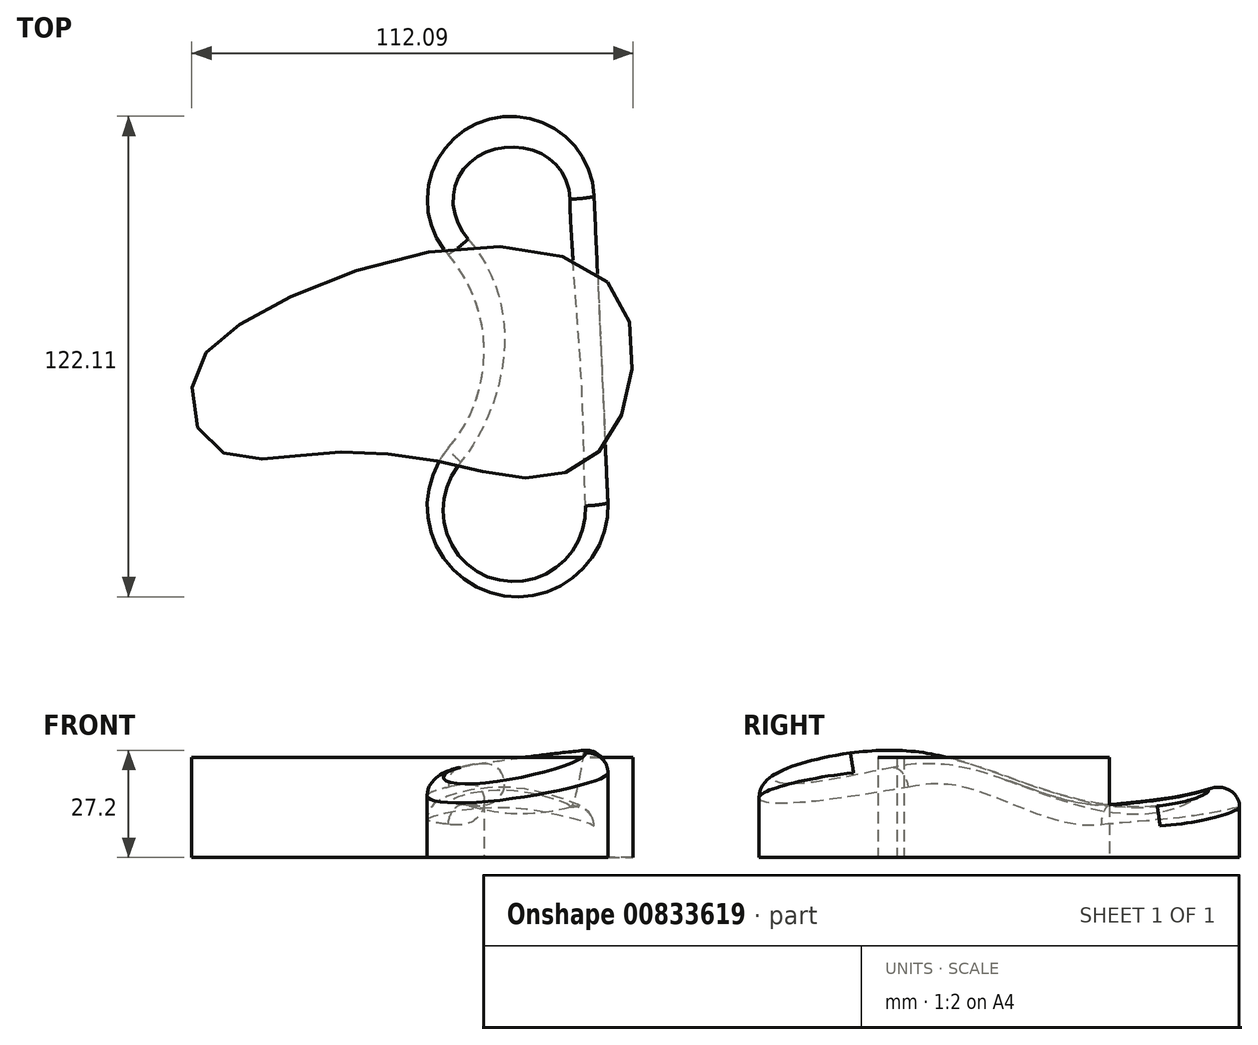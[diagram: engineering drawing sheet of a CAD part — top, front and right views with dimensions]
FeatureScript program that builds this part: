
annotation { "Feature Type Name" : "Feature", "Feature Type Description" : "" }
export const myFeature = defineFeature(function(context is Context, id is Id, definition is map)
    precondition{}
    {
        {
            var Q0;
            Q0=qCreatedBy(makeId("Right.planeOp"),FACE);
            cPlane(context, id + "F0", {"entities" : qUnion([Q0]), "cplaneType" : CPlaneType.OFFSET, "offset" : 25.4 * mm, "width" : 152.4 * mm, "height" : 152.4 * mm});
        }
        {
            var Q0;
            Q0=qCreatedBy(id+"F0.planeOp",FACE);
            cPlane(context, id + "F1", {"entities" : qUnion([Q0]), "cplaneType" : CPlaneType.OFFSET, "offset" : 25.4 * mm, "width" : 152.4 * mm, "height" : 152.4 * mm});
        }
        {
            var Q0;
            Q0=qCreatedBy(makeId("Right.planeOp"),FACE);
            var sketch = newSketch(context, id + "F2", { "sketchPlane" : qUnion([Q0])});
            skFitSpline(sketch, "E0", {"points": [v(-69.77, 10.75) * mm, v(-48.27, 16.65) * mm, v(-19.6, 21.71) * mm, v(13.28, 20.02) * mm, v(40.26, 17.5) * mm, v(69.77, 24.24) * mm], "startDerivative": vector(116.9, 33.43) * mm, "endDerivative": vector(144.91, 44.8) * mm});
            skLineSegment(sketch, "E1", {"start": v(-69.77, 10.75) * mm, "end": v(-69.77, 0) * mm});
            skLineSegment(sketch, "E2", {"start": v(-69.77, 0) * mm, "end": v(69.77, 0) * mm});
            skLineSegment(sketch, "E3", {"start": v(69.77, 0) * mm, "end": v(69.77, 24.24) * mm});
            skSolve(sketch);
        }
        {
            var Q0;
            Q0=qCreatedBy(id+"F0.planeOp",FACE);
            var sketch = newSketch(context, id + "F3", { "sketchPlane" : qUnion([Q0])});
            skFitSpline(sketch, "E4", {"points": [v(-68.93, 16.65) * mm, v(-47.43, 22.13) * mm, v(-15.8, 24.66) * mm, v(14.12, 15.39) * mm, v(43.63, 12.01) * mm, v(69.77, 30.14) * mm], "startDerivative": vector(115.8, 32.39) * mm, "endDerivative": vector(119.1, 112.04) * mm});
            skLineSegment(sketch, "E5", {"start": v(-68.93, 16.65) * mm, "end": v(-68.93, 0) * mm});
            skLineSegment(sketch, "E6", {"start": v(-68.93, 0) * mm, "end": v(69.77, 0) * mm});
            skLineSegment(sketch, "E7", {"start": v(69.77, 0) * mm, "end": v(69.77, 30.14) * mm});
            skSolve(sketch);
        }
        {
            var Q0;
            Q0=qCreatedBy(id+"F1.planeOp",FACE);
            var sketch = newSketch(context, id + "F4", { "sketchPlane" : qUnion([Q0])});
            skFitSpline(sketch, "E8", {"points": [v(-65.97, 22.55) * mm, v(-46.16, 25.93) * mm, v(-21.71, 27.61) * mm, v(12.44, 18.76) * mm, v(41.95, 15.8) * mm, v(70.19, 19.18) * mm], "startDerivative": vector(113.6, 19.12) * mm, "endDerivative": vector(138.59, 22.07) * mm});
            skLineSegment(sketch, "E9", {"start": v(-65.97, 0) * mm, "end": v(70.19, 0) * mm});
            skLineSegment(sketch, "E10", {"start": v(70.19, 0) * mm, "end": v(70.19, 19.18) * mm});
            skLineSegment(sketch, "E11", {"start": v(-65.97, 22.55) * mm, "end": v(-65.97, 0) * mm});
            skSolve(sketch);
        }
        {
            var Q0;
            Q0 = qSketchRegion(id + "F2", true);
            var Q1;
            Q1 = qSketchRegion(id + "F3", true);
            var Q2;
            Q2 = qSketchRegion(id + "F4", true);
            loft(context, id + "F5", {"sheetProfilesArray" : [{ "sheetProfileEntities" : qUnion([Q0]) }, { "sheetProfileEntities" : qUnion([Q1]) }, { "sheetProfileEntities" : qUnion([Q2]) }]});
        }
        {
            var Q0;
            Q0=qCreatedBy(makeId("Top.planeOp"),FACE);
            var sketch = newSketch(context, id + "F6", { "sketchPlane" : qUnion([Q0])});
            skArc(sketch, "E12", {"start": v(45.35, 41.6) * mm, "mid": v(16.31, 60.31) * mm, "end": v(8.2, 26.74) * mm});
            skArc(sketch, "E13", {"start": v(8.45, -22.4) * mm, "mid": v(18.47, -59.03) * mm, "end": v(48.87, -36.27) * mm});
            skArc(sketch, "E14", {"start": v(8.45, -22.4) * mm, "mid": v(17.46, 2.22) * mm, "end": v(8.2, 26.74) * mm});
            skLineSegment(sketch, "E15", {"start": v(45.35, 41.6) * mm, "end": v(48.87, -36.27) * mm});
            skSolve(sketch);
        }
        {
            var Q0;
            Q0 = qSketchRegion(id + "F6", true);
            extrude(context, id + "F7", {"entities" : qUnion([Q0]), "depth" : 30.48 * mm, "offsetDistance" : 25.4 * mm});
        }
        {
            var Q0;
            Q0=makeQuery(id+"F5.opLoft","SWEPT_BODY",BODY,{"disambiguationData":[OSD([makeQuery(id+"F2.imprint","IMPRINT",FACE,{"disambiguationData":[TD([[makeQuery(id+"F2.imprint","IMPRINT",EDGE,{"derivedFrom":sQuery(id+"F2.wireOp",EDGE,"E0")}),-1.0]])]}),sQuery(id+"F3.wireOp",EDGE,"E4"),makeQuery(id+"F4.imprint","IMPRINT",FACE,{"disambiguationData":[TD([[makeQuery(id+"F4.imprint","IMPRINT",EDGE,{"derivedFrom":sQuery(id+"F4.wireOp",EDGE,"E8")}),-1.0]])]})])]});
            var Q1;
            Q1=makeQuery(id+"F7.opExtrude","SWEPT_BODY",BODY,{"disambiguationData":[OSD([sQuery(id+"F6.wireOp",EDGE,"E12"),sQuery(id+"F6.wireOp",EDGE,"E13"),sQuery(id+"F6.wireOp",EDGE,"E14"),sQuery(id+"F6.wireOp",EDGE,"E15")])]});
            booleanBodies(context, id + "F8", {"operationType" : BooleanOperationType.INTERSECTION, "tools" : qUnion([Q0, Q1])});
        }
        {
            var Q0;
            Q0=makeQuery(id+"F8.opBoolean","INTERSECT",EDGE,{"derivedFrom":[makeQuery(id+"F5.opLoft","SWEPT_FACE",FACE,{"disambiguationData":[OSD([sQuery(id+"F2.wireOp",EDGE,"E0"),sQuery(id+"F2.wireOp",EDGE,"E1"),sQuery(id+"F2.wireOp",EDGE,"E3"),sQuery(id+"F3.wireOp",EDGE,"E4"),sQuery(id+"F3.wireOp",EDGE,"E5"),sQuery(id+"F3.wireOp",EDGE,"E7"),sQuery(id+"F4.wireOp",EDGE,"E8"),sQuery(id+"F4.wireOp",EDGE,"E10"),sQuery(id+"F4.wireOp",EDGE,"E11")])]}),makeQuery(id+"F7.opExtrude","SWEPT_FACE",FACE,{"disambiguationData":[OSD([sQuery(id+"F6.wireOp",EDGE,"E15")])]})]});
            fillet(context, id + "F9", {"entities" : qUnion([Q0]), "radius" : 5.08 * mm, "tangentPropagation" : true, "allowEdgeOverflow" : false});
        }
        {
            var Q0;
            Q0=qCreatedBy(makeId("Top.planeOp"),FACE);
            var sketch = newSketch(context, id + "F10", { "sketchPlane" : qUnion([Q0])});
            skFitSpline(sketch, "E16", {"points": [v(48.8, 19.72) * mm, v(54.98, -3.2) * mm, v(46.16, -23.93) * mm, v(29.4, -30.1) * mm, v(6.92, -26.13) * mm, v(-19.53, -23.49) * mm, v(-37.61, -25.25) * mm, v(-53.04, -20.84) * mm, v(-56.13, -4.09) * mm, v(-42.9, 10.02) * mm, v(8.68, 28.1) * mm, v(48.8, 19.72) * mm]});
            skSolve(sketch);
        }
        {
            var Q0;
            Q0 = qSketchRegion(id + "F10", true);
            extrude(context, id + "F11", {"entities" : qUnion([Q0]), "depth" : 25.4 * mm, "offsetDistance" : 25.4 * mm});
        }
    });
